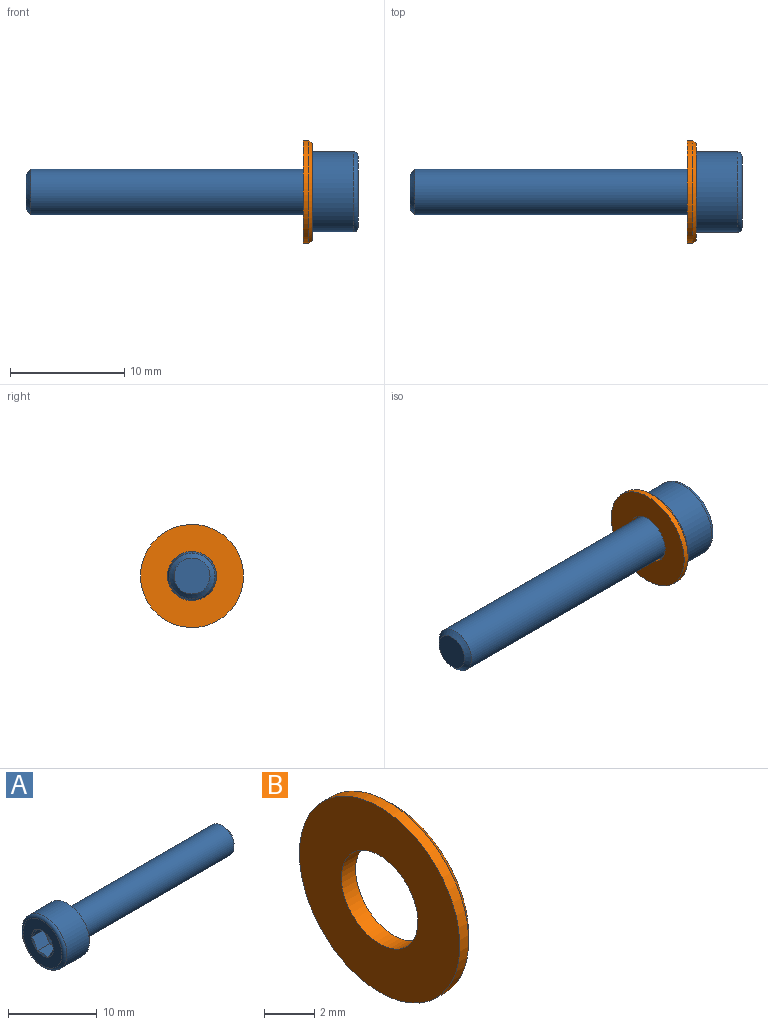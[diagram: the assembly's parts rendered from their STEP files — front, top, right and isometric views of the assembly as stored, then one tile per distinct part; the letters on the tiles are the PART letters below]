
ASSEMBLY  parts=2 mates=1
PART A: 24 faces, bbox 29x7.6x7.6 mm
  f0: plane 1.3x0.75mm, normal (-1,0,0), area 0.1mm2, adj f16,f17,f23
  f1: plane 1.5x0.43mm, normal (-1,0,0), area 0.1mm2, adj f17,f18,f23
  f2: plane 1.3x0.75mm, normal (-1,0,0), area 0.1mm2, adj f18,f19,f23
  f3: plane 1.3x0.75mm, normal (-1,0,0), area 0.1mm2, adj f19,f20,f23
  f4: plane 1.5x0.43mm, normal (-1,0,0), area 0.1mm2, adj f20,f21,f23
  f5: cone r=1.74mm half-angle=60deg, axis (-1,0,0), area 2mm2, adj f15,f16,f17,f18,f19,f20,f21
  f6: cone r=2.01mm half-angle=20.6deg, axis (-1,0,0), area 5.6mm2, adj f7,f11
  f7: torus R=2.2mm, axis (1,0,0), area 0.9mm2, adj f6,f10
  f8: plane 3.14x3.14mm, normal (1,0,0), area 7.7mm2, adj f9
  f9: cone r=2mm half-angle=45deg, axis (-1,0,0), area 6.8mm2, adj f8,f10
  f10: cylinder r=2mm len=23.97mm, axis (1,0,0), area 301.2mm2, adj f7,f9
  f11: torus R=2.35mm, axis (1,0,0), area 3.4mm2, adj f6,f13
  f12: cylinder r=3.5mm len=7mm, axis (1,0,0), area 79.2mm2, adj f13,f14
  f13: plane 7x7mm, normal (1,0,0), area 21.1mm2, adj f11,f12
  f14: torus R=3.1mm, axis (1,0,0), area 13.2mm2, adj f12,f15
  f15: plane 6.2x6.2mm, normal (-1,0,0), area 20.7mm2, adj f5,f14
  f16: plane 2x1.74mm, normal (0,0,-1), area 3.3mm2, adj f0,f5,f17,f21,f22
  f17: plane 2x1.5mm, normal (0,0.87,-0.5), area 3.3mm2, adj f0,f1,f5,f16,f18
  f18: plane 2x1.5mm, normal (0,0.87,0.5), area 3.3mm2, adj f1,f2,f5,f17,f19
  f19: plane 2x1.74mm, normal (0,0,1), area 3.3mm2, adj f2,f3,f5,f18,f20
  f20: plane 2x1.5mm, normal (0,-0.87,0.5), area 3.3mm2, adj f3,f4,f5,f19,f21
  f21: plane 2x1.5mm, normal (0,-0.87,-0.5), area 3.3mm2, adj f4,f5,f16,f20,f22
  f22: plane 1.3x0.75mm, normal (-1,0,0), area 0.1mm2, adj f16,f21,f23
  f23: cone r=1.5mm half-angle=60deg, axis (-1,0,0), area 8.2mm2, adj f0,f1,f2,f3,f4,f22
PART B: 5 faces, bbox 0.8x9x9 mm
  f0: plane 9x9mm, normal (-1,0,0), area 49.1mm2, adj f1,f4
  f1: cylinder r=2.15mm len=4.3mm, axis (1,0,0), area 10.8mm2, adj f0,f2
  f2: plane 8.4x8.4mm, normal (1,0,0), area 40.9mm2, adj f1,f3
  f3: cone r=4.2mm half-angle=45deg, axis (-1,0,0), area 11.6mm2, adj f2,f4
  f4: cylinder r=4.5mm len=9mm, axis (1,0,0), area 14.1mm2, adj f0,f3
PLACE A rot(axis=(0,1,0),180deg) t=(0.8,0,0)mm
PLACE B at identity fixed
MATE fastened A.f5 <-> B.f1  axis (-1,0,0) through (0.8,0,0)mm
